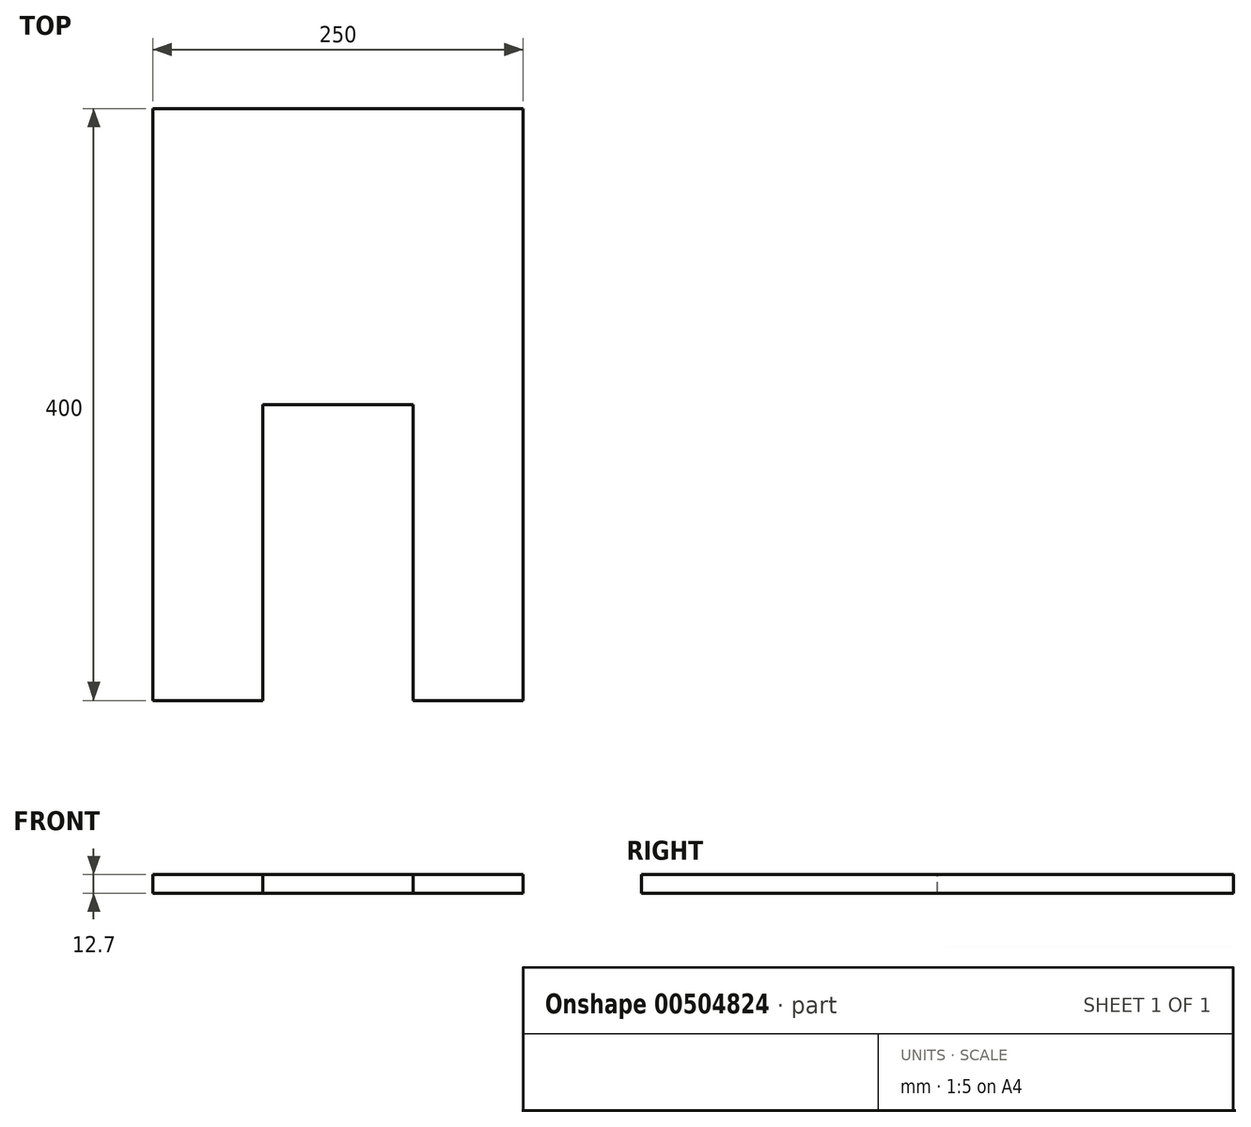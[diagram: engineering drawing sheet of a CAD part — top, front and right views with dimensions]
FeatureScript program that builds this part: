
annotation { "Feature Type Name" : "Feature", "Feature Type Description" : "" }
export const myFeature = defineFeature(function(context is Context, id is Id, definition is map)
    precondition{}
    {
        {
            var Q0;
            Q0=qCreatedBy(makeId("Top.planeOp"),FACE);
            var sketch = newSketch(context, id + "F0", { "sketchPlane" : qUnion([Q0])});
            skLineSegment(sketch, "E0.bottom", {"start": v(-132.36, -149.16) * mm, "end": v(117.64, -149.16) * mm});
            skLineSegment(sketch, "E0.top", {"start": v(-132.36, 250.84) * mm, "end": v(117.64, 250.84) * mm});
            skLineSegment(sketch, "E0.left", {"start": v(-132.36, -149.16) * mm, "end": v(-132.36, 250.84) * mm});
            skLineSegment(sketch, "E0.right", {"start": v(117.64, -149.16) * mm, "end": v(117.64, 250.84) * mm});
            skSolve(sketch);
        }
        {
            var Q0;
            Q0 = qSketchRegion(id + "F0", true);
            var sketch = newSketch(context, id + "F1", { "sketchPlane" : qUnion([Q0])});
            skSolve(sketch);
        }
        {
            var Q0;
            Q0=makeQuery(id+"F1.imprint","IMPRINT",FACE,{"disambiguationData":[TD([[makeQuery(id+"F1.imprint","IMPRINT",EDGE,{"derivedFrom":makeQuery(id+"F0.imprint","IMPRINT",EDGE,{"derivedFrom":sQuery(id+"F0.wireOp",EDGE,"E0.bottom")})}),1.0]])]});
            extrude(context, id + "F2", {"entities" : qUnion([Q0]), "depth" : 12.7 * mm});
        }
        {
            var Q0;
            Q0=makeQuery(id+"F2.opExtrude","CAP_FACE",FACE,{"disambiguationData":[OSD([sQuery(id+"F0.wireOp",EDGE,"E0.bottom"),sQuery(id+"F0.wireOp",EDGE,"E0.top"),sQuery(id+"F0.wireOp",EDGE,"E0.left"),sQuery(id+"F0.wireOp",EDGE,"E0.right")])],"isStart":false});
            var sketch = newSketch(context, id + "F3", { "sketchPlane" : qUnion([Q0])});
            skLineSegment(sketch, "E1.0", {"start": v(43.44, -149.16) * mm, "end": v(43.44, 50.84) * mm});
            skLineSegment(sketch, "E2.0", {"start": v(-58.16, -149.16) * mm, "end": v(-58.16, 50.84) * mm});
            skLineSegment(sketch, "E3", {"start": v(-58.16, 50.84) * mm, "end": v(43.44, 50.84) * mm});
            skLineSegment(sketch, "E4", {"start": v(-58.16, -149.16) * mm, "end": v(43.44, -149.16) * mm});
            skSolve(sketch);
        }
        {
            var Q0;
            Q0=makeQuery(id+"F3.imprint","IMPRINT",FACE,{"disambiguationData":[TD([[makeQuery(id+"F3.imprint","IMPRINT",EDGE,{"derivedFrom":sQuery(id+"F3.wireOp",EDGE,"E1.0")}),1.0]])]});
            extrude(context, id + "F4", {"entities" : qUnion([Q0]), "operationType" : NewBodyOperationType.REMOVE, "oppositeDirection" : true, "depth" : 25.4 * mm});
        }
    });
